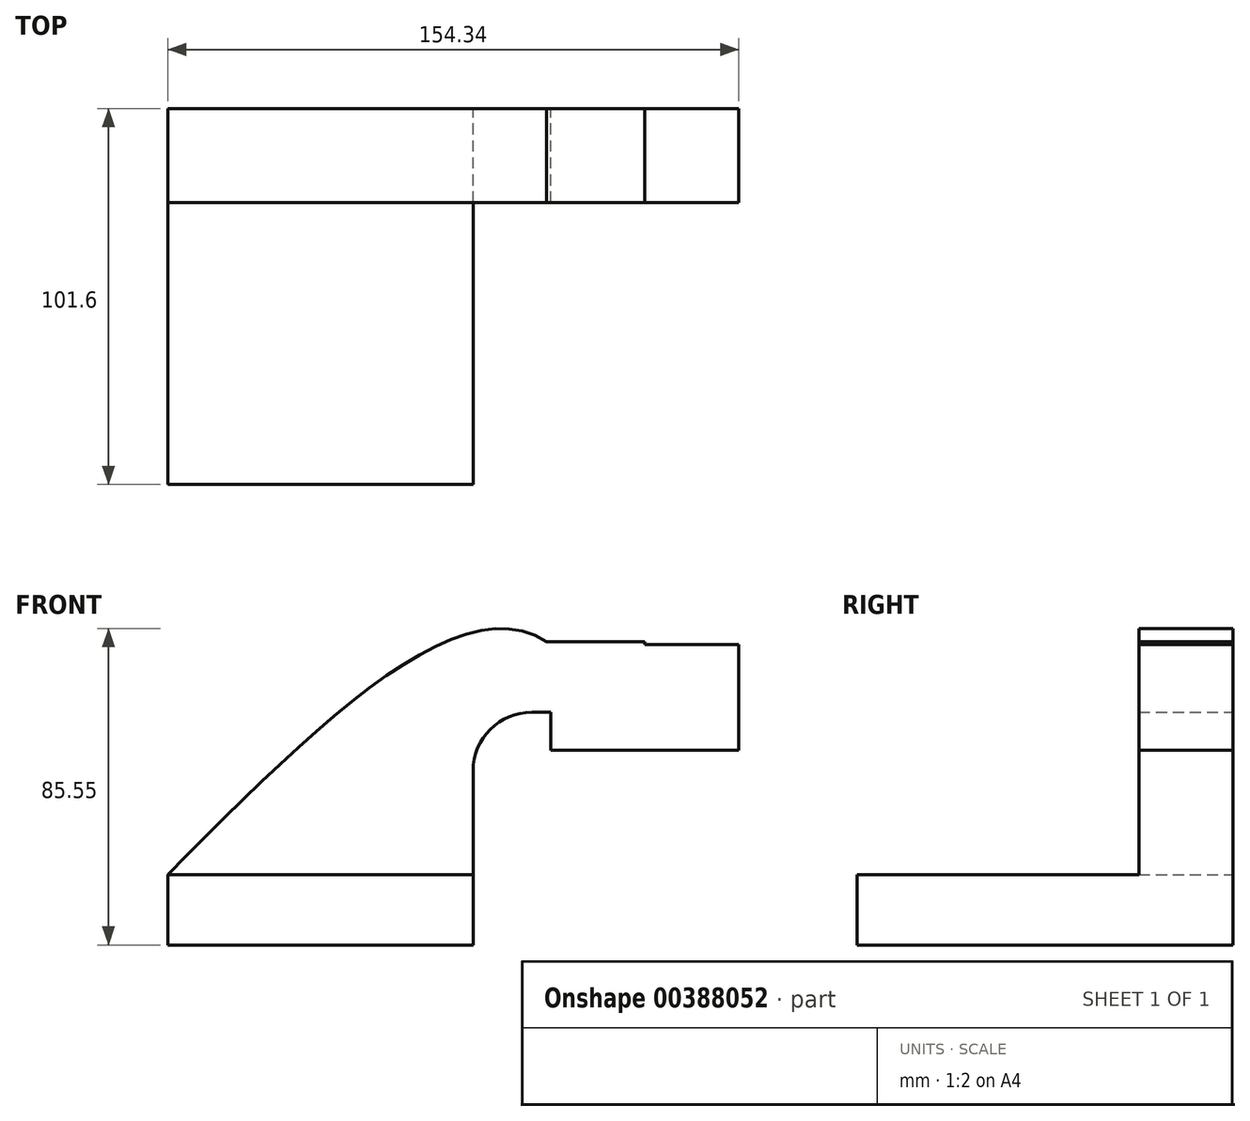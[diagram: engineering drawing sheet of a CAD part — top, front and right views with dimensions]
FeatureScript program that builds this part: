
annotation { "Feature Type Name" : "Feature", "Feature Type Description" : "" }
export const myFeature = defineFeature(function(context is Context, id is Id, definition is map)
    precondition{}
    {
        {
            var Q0;
            Q0=qCreatedBy(makeId("Front.planeOp"),FACE);
            var sketch = newSketch(context, id + "F0", { "sketchPlane" : qUnion([Q0])});
            skLineSegment(sketch, "E0.bottom", {"start": v(41.28, -9.52) * mm, "end": v(-41.28, -9.53) * mm});
            skLineSegment(sketch, "E0.top", {"start": v(41.28, 9.53) * mm, "end": v(-41.28, 9.53) * mm});
            skLineSegment(sketch, "E0.left", {"start": v(41.28, -9.52) * mm, "end": v(41.28, 9.53) * mm});
            skLineSegment(sketch, "E0.right", {"start": v(-41.28, -9.53) * mm, "end": v(-41.28, 9.53) * mm});
            skPoint(sketch, "E0.middle", {"position": v(0, 0) * mm});
            skLineSegment(sketch, "E1.bottom", {"start": v(113.06, 43.14) * mm, "end": v(62.26, 43.14) * mm});
            skLineSegment(sketch, "E1.top", {"start": v(113.06, 71.71) * mm, "end": v(62.26, 71.71) * mm});
            skLineSegment(sketch, "E1.left", {"start": v(113.06, 43.14) * mm, "end": v(113.06, 71.71) * mm});
            skLineSegment(sketch, "E1.right", {"start": v(62.26, 43.14) * mm, "end": v(62.26, 71.71) * mm});
            skPoint(sketch, "E1.middle", {"position": v(87.66, 57.42) * mm});
            skLineSegment(sketch, "E2", {"start": v(41.28, 9.53) * mm, "end": v(41.28, 37.53) * mm});
            skArc(sketch, "E3", {"start": v(41.27, 37.53) * mm, "mid": v(45.92, 48.75) * mm, "end": v(57.15, 53.4) * mm});
            skLineSegment(sketch, "E4", {"start": v(57.15, 53.4) * mm, "end": v(87.63, 53.4) * mm});
            skLineSegment(sketch, "E5.0", {"start": v(57.15, 72.45) * mm, "end": v(87.63, 72.45) * mm});
            skArc(sketch, "E5.1", {"start": v(22.23, 37.53) * mm, "mid": v(32.45, 62.22) * mm, "end": v(57.15, 72.45) * mm});
            skLineSegment(sketch, "E5.2", {"start": v(22.23, 9.53) * mm, "end": v(22.23, 37.53) * mm});
            skLineSegment(sketch, "E6", {"start": v(87.63, 72.45) * mm, "end": v(87.63, 43.14) * mm});
            skFitSpline(sketch, "E7", {"points": [v(-41.28, 9.53) * mm, v(62.26, 71.71) * mm, v(87.51, 9.53) * mm, v(86.25, 9.53) * mm], "startDerivative": vector(220.09, 221.36) * mm, "endDerivative": vector(-26.61, 14.06) * mm});
            skSolve(sketch);
        }
        {
            var Q0;
            Q0=makeQuery(id+"F0.imprint","IMPRINT",FACE,{"disambiguationData":[TD([[makeQuery(id+"F0.imprint","IMPRINT",EDGE,{"derivedFrom":sQuery(id+"F0.wireOp",EDGE,"E0.bottom")}),-1.0]])]});
            extrude(context, id + "F1", {"entities" : qUnion([Q0]), "depth" : 101.6 * mm});
        }
        {
            var Q0;
            Q0 = qSketchRegion(id + "F0", true);
            extrude(context, id + "F2", {"entities" : qUnion([Q0]), "operationType" : NewBodyOperationType.ADD, "depth" : 25.4 * mm});
        }
    });
